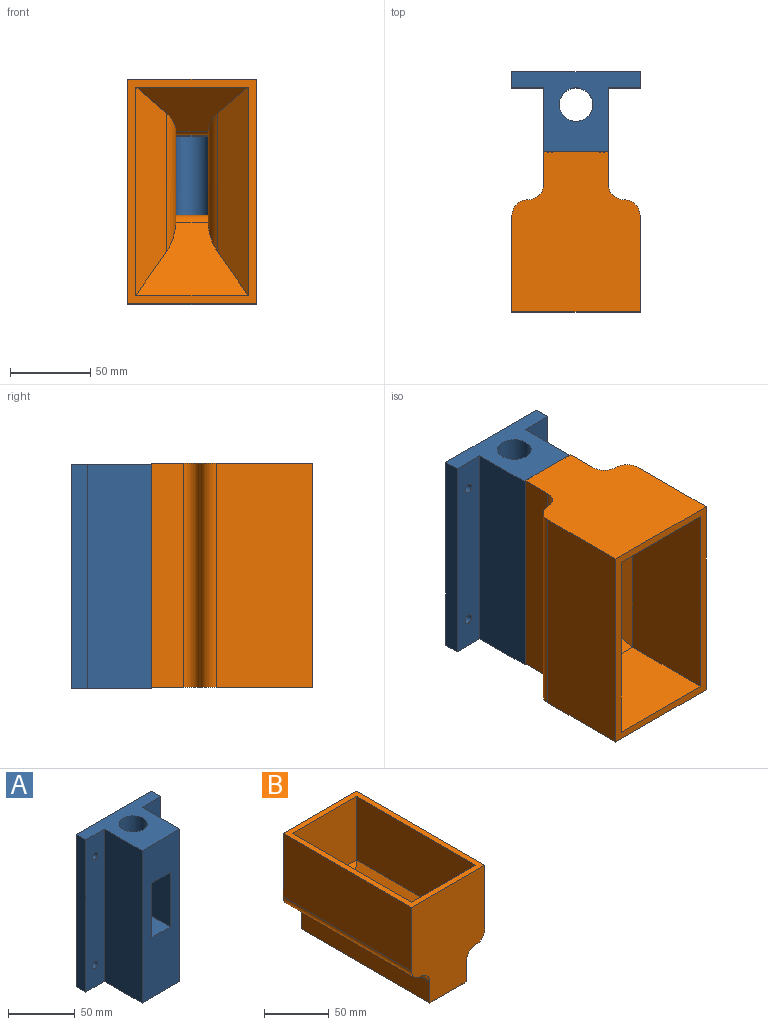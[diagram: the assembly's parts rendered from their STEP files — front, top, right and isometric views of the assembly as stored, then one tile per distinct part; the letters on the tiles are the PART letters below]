
ASSEMBLY  parts=2 mates=1
PART A: 21 faces, bbox 80x50x140 mm
  f0: plane 140x20mm, normal (0,-1,0), area 2743.5mm2, adj f1,f2,f3,f5,f8,f16
  f1: plane 80x50mm, normal (0,0,-1), area 2053.6mm2, adj f0,f2,f4,f9,f10,f11,f16,f17
  f2: plane 140x10mm, normal (1,0,0), area 1400mm2, adj f0,f1,f3,f10
  f3: plane 80x50mm, normal (0,0,1), area 2053.6mm2, adj f0,f2,f4,f9,f10,f11,f16,f17
  f4: plane 140x10mm, normal (-1,0,0), area 1400mm2, adj f1,f3,f9,f10
  f5: cylinder r=3mm len=10mm, axis (0,1,0), area 188.5mm2, adj f0,f10
  f6: cylinder r=3mm len=10mm, axis (0,1,0), area 188.5mm2, adj f9,f10
  f7: cylinder r=3mm len=10mm, axis (0,1,0), area 188.5mm2, adj f9,f10
  f8: cylinder r=3mm len=10mm, axis (0,1,0), area 188.5mm2, adj f0,f10
  f9: plane 140x20mm, normal (0,-1,0), area 2743.5mm2, adj f1,f3,f4,f6,f7,f11
  f10: plane 140x80mm, normal (0,1,0), area 11086.9mm2, adj f1,f2,f3,f4,f5,f6,f7,f8
  f11: plane 140x40mm, normal (-1,0,0), area 5600mm2, adj f1,f3,f9,f17
  f12: plane 26.3x20mm, normal (0,0,-1), area 419mm2, adj f13,f15,f17,f18
  f13: plane 65x26.3mm, normal (-1,0,0), area 1335.3mm2, adj f12,f14,f17,f18,f19,f20
  f14: plane 22.11x20mm, normal (0,0,1), area 371.6mm2, adj f13,f15,f17,f20
  f15: plane 65x26.3mm, normal (1,0,0), area 1335.3mm2, adj f12,f14,f17,f18,f19,f20
  f16: plane 140x40mm, normal (1,0,0), area 5600mm2, adj f0,f1,f3,f17
  f17: plane 140x40mm, normal (0,-1,0), area 4600mm2, adj f1,f3,f11,f12,f13,f14,f15,f16
  f18: cylinder r=10.5mm len=140mm, axis (0,0,-1), area 7515.1mm2, adj f1,f3,f12,f13,f15,f19
  f19: cone r=11.5mm half-angle=3.8deg, axis (0,0,1), area 355.9mm2, adj f13,f15,f18,f20
  f20: torus R=12.44mm, axis (0,0,-1), area 35.9mm2, adj f13,f14,f15,f19
PART B: 43 faces, bbox 80x140x100 mm
  f0: plane 140x2mm, normal (0,0,-1), area 280mm2, adj f4,f5,f39,f40
  f1: plane 140x29.6mm, normal (0,0,-1), area 3144mm2, adj f4,f5,f6,f7,f8,f29,f34,f37
  f2: plane 140x2mm, normal (0,0,-1), area 280mm2, adj f4,f5,f31,f35
  f3: plane 140x2mm, normal (0,0,-1), area 280mm2, adj f4,f5,f10,f32
  f4: plane 100x80mm, normal (0,-1,0), area 6798.6mm2, adj f0,f1,f2,f3,f9,f10,f11,f12
  f5: plane 100x80mm, normal (0,1,0), area 6798.6mm2, adj f0,f1,f2,f3,f9,f10,f11,f12
  f6: plane 54.38x6.72mm, normal (1,0,0), area 344.6mm2, adj f1,f7,f27,f29,f30
  f7: plane 20x1.3mm, normal (0,-1,0), area 26mm2, adj f1,f6,f8,f30
  f8: plane 54.38x6.72mm, normal (-1,0,0), area 344.6mm2, adj f1,f7,f28,f29,f30
  f9: plane 140x80mm, normal (0,0,1), area 2100mm2, adj f4,f5,f13,f14,f19,f20,f21,f22
  f10: plane 140x20mm, normal (-1,0,0), area 2800mm2, adj f3,f4,f5,f15
  f11: plane 140x20mm, normal (1,0,0), area 2800mm2, adj f4,f5,f12,f16
  f12: plane 140x2mm, normal (0,0,-1), area 280mm2, adj f4,f5,f11,f42
  f13: plane 140x60mm, normal (1,0,0), area 8400mm2, adj f4,f5,f9,f18
  f14: plane 140x60mm, normal (-1,0,0), area 8400mm2, adj f4,f5,f9,f17
  f15: cylinder r=10mm len=140mm, axis (0,1,0), area 2199.1mm2, adj f4,f5,f10,f17
  f16: cylinder r=10mm len=140mm, axis (0,-1,0), area 2199.1mm2, adj f4,f5,f11,f18
  f17: cylinder r=10mm len=140mm, axis (0,1,0), area 2199.1mm2, adj f4,f5,f14,f15
  f18: cylinder r=10mm len=140mm, axis (0,-1,0), area 2199.1mm2, adj f4,f5,f13,f16
  f19: plane 70x60mm, normal (0,1,0), area 4200mm2, adj f9,f20,f22,f24
  f20: plane 130x60mm, normal (-1,0,0), area 7800mm2, adj f9,f19,f21,f25
  f21: plane 70x60mm, normal (0,-1,0), area 4200mm2, adj f9,f20,f22,f23
  f22: plane 130x60mm, normal (1,0,0), area 7800mm2, adj f9,f19,f21,f26
  f23: plane 70x32.19mm, normal (0,-0.76,0.65), area 1693.8mm2, adj f21,f25,f26,f27,f28,f30
  f24: plane 70x45.74mm, normal (0,0.57,0.82), area 2236.4mm2, adj f19,f25,f26,f27,f28,f29
  f25: plane 130x19.14mm, normal (-0.71,0,0.71), area 2927mm2, adj f20,f23,f24,f28
  f26: plane 130x19.14mm, normal (0.71,0,0.71), area 2927mm2, adj f22,f23,f24,f27
  f27: cylinder r=20mm len=86.25mm, axis (0,1,0), area 1115mm2, adj f6,f23,f24,f26,f29,f30
  f28: cylinder r=20mm len=86.25mm, axis (0,-1,0), area 1115mm2, adj f8,f23,f24,f25,f29,f30
  f29: cylinder r=10mm len=20.08mm, axis (1,0,0), area 187.9mm2, adj f1,f6,f8,f24,f27,f28
  f30: cylinder r=10mm len=20.06mm, axis (1,0,0), area 141.8mm2, adj f6,f7,f8,f23,f27,f28
  f31: plane 140x0.6mm, normal (-1,0,0), area 84mm2, adj f2,f4,f5,f33
  f32: plane 140x0.6mm, normal (1,0,0), area 84mm2, adj f3,f4,f5,f33
  f33: plane 140x0.6mm, normal (0,0,-1), area 84mm2, adj f4,f5,f31,f32
  f34: plane 140x0.6mm, normal (-1,0,0), area 84mm2, adj f1,f4,f5,f36
  f35: plane 140x0.6mm, normal (1,0,0), area 84mm2, adj f2,f4,f5,f36
  f36: plane 140x0.6mm, normal (0,0,-1), area 84mm2, adj f4,f5,f34,f35
  f37: plane 140x0.6mm, normal (1,0,0), area 84mm2, adj f1,f4,f5,f38
  f38: plane 140x0.6mm, normal (0,0,-1), area 84mm2, adj f4,f5,f37,f39
  f39: plane 140x0.6mm, normal (-1,0,0), area 84mm2, adj f0,f4,f5,f38
  f40: plane 140x0.6mm, normal (1,0,0), area 84mm2, adj f0,f4,f5,f41
  f41: plane 140x0.6mm, normal (0,0,-1), area 84mm2, adj f4,f5,f40,f42
  f42: plane 140x0.6mm, normal (-1,0,0), area 84mm2, adj f4,f5,f12,f41
PLACE A t=(-30.46,-0.64,-12.08)mm fixed
PLACE B rot(axis=(1,0,0),90deg) t=(-30.46,-50.64,-11.08)mm
MATE fastened A.f17 <-> B.f1  axis (0,-1,0) through (-30.46,-50.64,-14.26)mm
